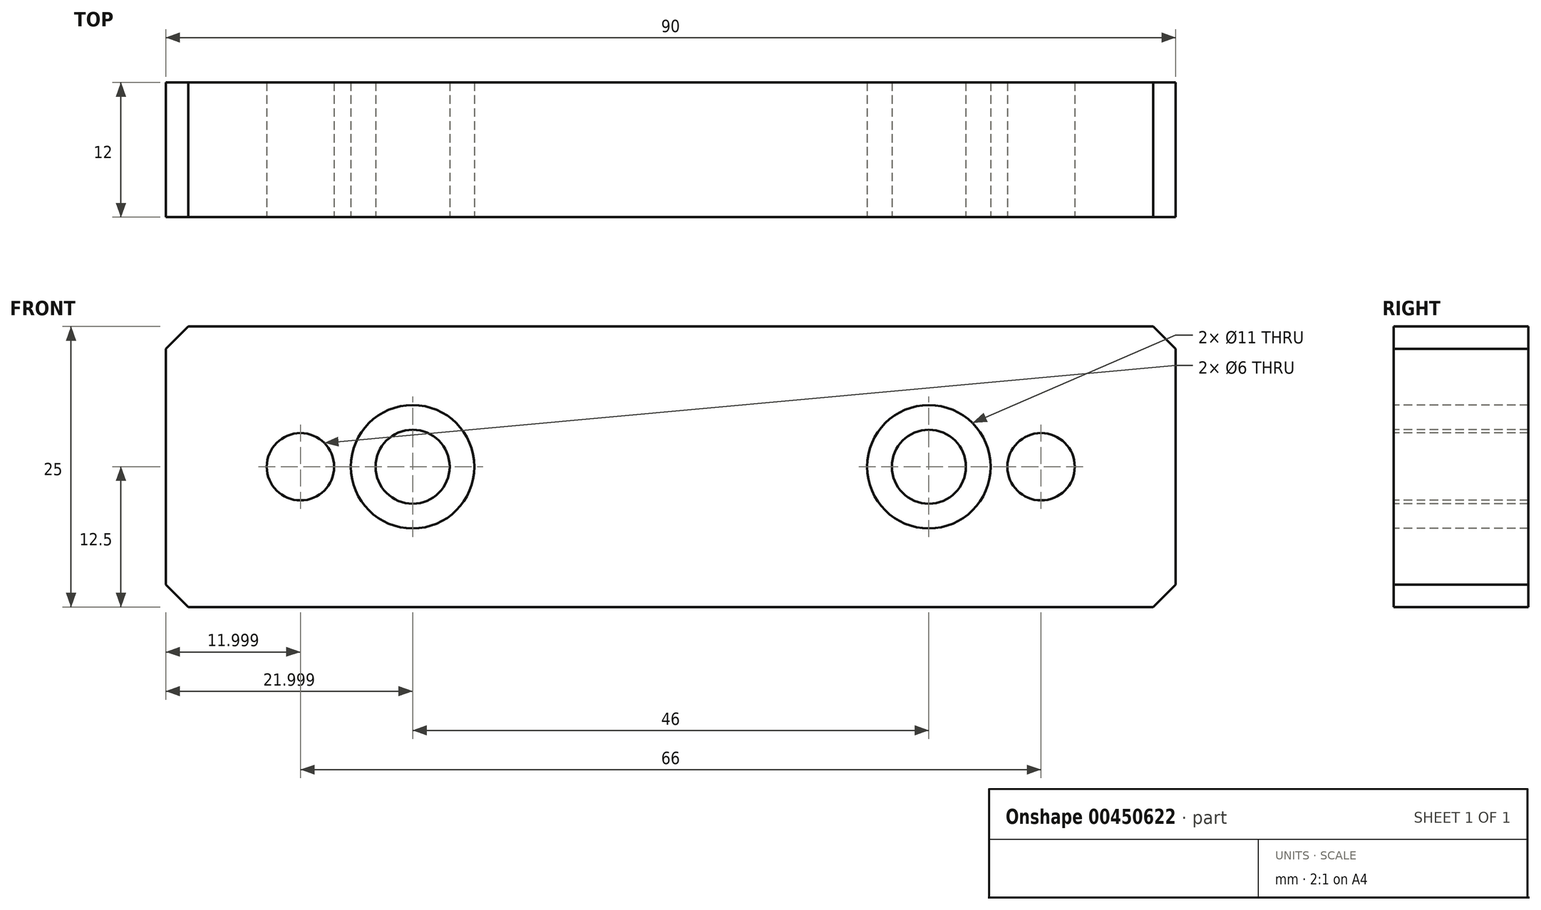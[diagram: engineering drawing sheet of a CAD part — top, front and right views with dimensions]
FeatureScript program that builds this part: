
annotation { "Feature Type Name" : "Feature", "Feature Type Description" : "" }
export const myFeature = defineFeature(function(context is Context, id is Id, definition is map)
    precondition{}
    {
        {
            var Q0;
            Q0=qCreatedBy(makeId("Front.planeOp"),FACE);
            var sketch = newSketch(context, id + "F0", { "sketchPlane" : qUnion([Q0])});
            skLineSegment(sketch, "E0", {"start": v(88.15, -90.29) * mm, "end": v(88.15, -111.29) * mm});
            skLineSegment(sketch, "E1", {"start": v(90.15, -88.29) * mm, "end": v(88.15, -90.29) * mm});
            skLineSegment(sketch, "E2", {"start": v(90.15, -113.29) * mm, "end": v(88.15, -111.29) * mm});
            skLineSegment(sketch, "E3", {"start": v(176.15, -88.29) * mm, "end": v(90.15, -88.29) * mm});
            skLineSegment(sketch, "E4", {"start": v(178.15, -90.29) * mm, "end": v(176.15, -88.29) * mm});
            skLineSegment(sketch, "E5", {"start": v(90.15, -113.29) * mm, "end": v(176.15, -113.29) * mm});
            skLineSegment(sketch, "E6", {"start": v(178.15, -111.29) * mm, "end": v(176.15, -113.29) * mm});
            skLineSegment(sketch, "E7", {"start": v(178.15, -111.29) * mm, "end": v(178.15, -90.29) * mm});
            skLineSegment(sketch, "E8", {"start": v(250.57, -113.29) * mm, "end": v(250.57, -88.29) * mm});
            skLineSegment(sketch, "E9", {"start": v(250.57, -88.29) * mm, "end": v(238.57, -88.29) * mm});
            skLineSegment(sketch, "E10", {"start": v(250.57, -113.29) * mm, "end": v(238.57, -113.29) * mm});
            skLineSegment(sketch, "E11", {"start": v(238.57, -88.29) * mm, "end": v(238.57, -113.29) * mm});
            skLineSegment(sketch, "E12", {"start": v(235.15, -100.79) * mm, "end": v(253.2, -100.79) * mm});
            skLineSegment(sketch, "E13", {"start": v(170.65, -100.79) * mm, "end": v(161.65, -100.79) * mm});
            skCircle(sketch, "E14", {"center": v(166.15, -100.79) * mm, "radius": 3 * mm});
            skLineSegment(sketch, "E15", {"start": v(166.15, -105.29) * mm, "end": v(166.15, -96.29) * mm});
            skCircle(sketch, "E16", {"center": v(166.15, -100.79) * mm, "radius": 2.46 * mm});
            skLineSegment(sketch, "E17", {"start": v(104.65, -100.79) * mm, "end": v(95.65, -100.79) * mm});
            skCircle(sketch, "E18", {"center": v(100.15, -100.79) * mm, "radius": 3 * mm});
            skLineSegment(sketch, "E19", {"start": v(100.15, -105.29) * mm, "end": v(100.15, -96.29) * mm});
            skCircle(sketch, "E20", {"center": v(100.15, -100.79) * mm, "radius": 2.46 * mm});
            skLineSegment(sketch, "E21", {"start": v(147.9, -100.79) * mm, "end": v(164.4, -100.79) * mm});
            skCircle(sketch, "E22", {"center": v(156.15, -100.79) * mm, "radius": 5.5 * mm});
            skLineSegment(sketch, "E23", {"start": v(156.15, -92.54) * mm, "end": v(156.15, -109.04) * mm});
            skCircle(sketch, "E24", {"center": v(156.15, -100.79) * mm, "radius": 3.3 * mm});
            skLineSegment(sketch, "E25", {"start": v(101.9, -100.79) * mm, "end": v(118.4, -100.79) * mm});
            skCircle(sketch, "E26", {"center": v(110.15, -100.79) * mm, "radius": 5.5 * mm});
            skLineSegment(sketch, "E27", {"start": v(110.15, -92.54) * mm, "end": v(110.15, -109.04) * mm});
            skCircle(sketch, "E28", {"center": v(110.15, -100.79) * mm, "radius": 3.3 * mm});
            skLineSegment(sketch, "E29", {"start": v(-261.09, -171.15) * mm, "end": v(-440.18, -171.15) * mm});
            skLineSegment(sketch, "E30", {"start": v(-440.18, -171.15) * mm, "end": v(-440.18, -94.4) * mm});
            skLineSegment(sketch, "E31", {"start": v(-440.18, -94.4) * mm, "end": v(-261.09, -94.4) * mm});
            skLineSegment(sketch, "E32", {"start": v(-261.09, -94.4) * mm, "end": v(-261.09, -171.15) * mm});
            skSolve(sketch);
        }
        {
            var Q0;
            Q0=makeQuery(id+"F0.imprint","IMPRINT",FACE,{"disambiguationData":[TD([[makeQuery(id+"F0.imprint","IMPRINT",EDGE,{"derivedFrom":sQuery(id+"F0.wireOp",EDGE,"E0")}),1.0]])]});
            var Q1;
            {var subQ0=sQuery(id+"F0.wireOp",EDGE,"E22");var subQ1=sQuery(id+"F0.wireOp",EDGE,"E21");var subQ2=makeQuery(id+"F0.imprint","INTERSECT",VERTEX,{"disambiguationData":[OD(1.0)],"derivedFrom":[subQ1,subQ0]});Q1=makeQuery(id+"F0.imprint","IMPRINT",FACE,{"disambiguationData":[TD([[makeQuery(id+"F0.imprint","IMPRINT",EDGE,{"disambiguationData":[TD([[subQ2,1.0]])],"derivedFrom":subQ1}),1.0]])]});}
            var Q2;
            {var subQ0=sQuery(id+"F0.wireOp",EDGE,"E22");var subQ1=sQuery(id+"F0.wireOp",EDGE,"E21");var subQ2=makeQuery(id+"F0.imprint","INTERSECT",VERTEX,{"disambiguationData":[OD(0.0)],"derivedFrom":[subQ1,subQ0]});Q2=makeQuery(id+"F0.imprint","IMPRINT",FACE,{"disambiguationData":[TD([[makeQuery(id+"F0.imprint","IMPRINT",EDGE,{"disambiguationData":[TD([[subQ2,-1.0]])],"derivedFrom":subQ1}),1.0]])]});}
            var Q3;
            {var subQ0=sQuery(id+"F0.wireOp",EDGE,"E22");var subQ1=sQuery(id+"F0.wireOp",EDGE,"E21");var subQ2=makeQuery(id+"F0.imprint","INTERSECT",VERTEX,{"disambiguationData":[OD(1.0)],"derivedFrom":[subQ1,subQ0]});Q3=makeQuery(id+"F0.imprint","IMPRINT",FACE,{"disambiguationData":[TD([[makeQuery(id+"F0.imprint","IMPRINT",EDGE,{"disambiguationData":[TD([[subQ2,1.0]])],"derivedFrom":subQ1}),-1.0]])]});}
            var Q4;
            {var subQ0=sQuery(id+"F0.wireOp",EDGE,"E23");var subQ1=sQuery(id+"F0.wireOp",EDGE,"E21");var subQ2=makeQuery(id+"F0.imprint","INTERSECT",VERTEX,{"derivedFrom":[subQ1,subQ0]});Q4=makeQuery(id+"F0.imprint","IMPRINT",FACE,{"disambiguationData":[TD([[makeQuery(id+"F0.imprint","IMPRINT",EDGE,{"disambiguationData":[TD([[subQ2,-1.0]])],"derivedFrom":subQ1}),1.0]])]});}
            var Q5;
            {var subQ0=sQuery(id+"F0.wireOp",EDGE,"E23");var subQ1=sQuery(id+"F0.wireOp",EDGE,"E21");var subQ2=makeQuery(id+"F0.imprint","INTERSECT",VERTEX,{"derivedFrom":[subQ1,subQ0]});Q5=makeQuery(id+"F0.imprint","IMPRINT",FACE,{"disambiguationData":[TD([[makeQuery(id+"F0.imprint","IMPRINT",EDGE,{"disambiguationData":[TD([[subQ2,-1.0]])],"derivedFrom":subQ1}),-1.0]])]});}
            var Q6;
            {var subQ0=sQuery(id+"F0.wireOp",EDGE,"E24");var subQ1=sQuery(id+"F0.wireOp",EDGE,"E21");var subQ2=makeQuery(id+"F0.imprint","INTERSECT",VERTEX,{"disambiguationData":[OD(0.0)],"derivedFrom":[subQ1,subQ0]});Q6=makeQuery(id+"F0.imprint","IMPRINT",FACE,{"disambiguationData":[TD([[makeQuery(id+"F0.imprint","IMPRINT",EDGE,{"disambiguationData":[TD([[subQ2,-1.0]])],"derivedFrom":subQ1}),1.0]])]});}
            var Q7;
            {var subQ0=sQuery(id+"F0.wireOp",EDGE,"E24");var subQ1=sQuery(id+"F0.wireOp",EDGE,"E21");var subQ2=makeQuery(id+"F0.imprint","INTERSECT",VERTEX,{"disambiguationData":[OD(0.0)],"derivedFrom":[subQ1,subQ0]});Q7=makeQuery(id+"F0.imprint","IMPRINT",FACE,{"disambiguationData":[TD([[makeQuery(id+"F0.imprint","IMPRINT",EDGE,{"disambiguationData":[TD([[subQ2,-1.0]])],"derivedFrom":subQ1}),-1.0]])]});}
            var Q8;
            {var subQ0=sQuery(id+"F0.wireOp",EDGE,"E22");var subQ1=sQuery(id+"F0.wireOp",EDGE,"E21");var subQ2=makeQuery(id+"F0.imprint","INTERSECT",VERTEX,{"disambiguationData":[OD(0.0)],"derivedFrom":[subQ1,subQ0]});Q8=makeQuery(id+"F0.imprint","IMPRINT",FACE,{"disambiguationData":[TD([[makeQuery(id+"F0.imprint","IMPRINT",EDGE,{"disambiguationData":[TD([[subQ2,-1.0]])],"derivedFrom":subQ1}),-1.0]])]});}
            var Q9;
            {var subQ0=sQuery(id+"F0.wireOp",EDGE,"E27");var subQ1=sQuery(id+"F0.wireOp",EDGE,"E25");var subQ2=makeQuery(id+"F0.imprint","INTERSECT",VERTEX,{"derivedFrom":[subQ1,subQ0]});Q9=makeQuery(id+"F0.imprint","IMPRINT",FACE,{"disambiguationData":[TD([[makeQuery(id+"F0.imprint","IMPRINT",EDGE,{"disambiguationData":[TD([[subQ2,-1.0]])],"derivedFrom":subQ1}),1.0]])]});}
            var Q10;
            {var subQ0=sQuery(id+"F0.wireOp",EDGE,"E26");var subQ1=sQuery(id+"F0.wireOp",EDGE,"E25");var subQ2=makeQuery(id+"F0.imprint","INTERSECT",VERTEX,{"disambiguationData":[OD(1.0)],"derivedFrom":[subQ1,subQ0]});Q10=makeQuery(id+"F0.imprint","IMPRINT",FACE,{"disambiguationData":[TD([[makeQuery(id+"F0.imprint","IMPRINT",EDGE,{"disambiguationData":[TD([[subQ2,1.0]])],"derivedFrom":subQ1}),-1.0]])]});}
            var Q11;
            {var subQ0=sQuery(id+"F0.wireOp",EDGE,"E27");var subQ1=sQuery(id+"F0.wireOp",EDGE,"E25");var subQ2=makeQuery(id+"F0.imprint","INTERSECT",VERTEX,{"derivedFrom":[subQ1,subQ0]});Q11=makeQuery(id+"F0.imprint","IMPRINT",FACE,{"disambiguationData":[TD([[makeQuery(id+"F0.imprint","IMPRINT",EDGE,{"disambiguationData":[TD([[subQ2,-1.0]])],"derivedFrom":subQ1}),-1.0]])]});}
            var Q12;
            {var subQ0=sQuery(id+"F0.wireOp",EDGE,"E26");var subQ1=sQuery(id+"F0.wireOp",EDGE,"E25");var subQ2=makeQuery(id+"F0.imprint","INTERSECT",VERTEX,{"disambiguationData":[OD(1.0)],"derivedFrom":[subQ1,subQ0]});Q12=makeQuery(id+"F0.imprint","IMPRINT",FACE,{"disambiguationData":[TD([[makeQuery(id+"F0.imprint","IMPRINT",EDGE,{"disambiguationData":[TD([[subQ2,1.0]])],"derivedFrom":subQ1}),1.0]])]});}
            var Q13;
            {var subQ0=sQuery(id+"F0.wireOp",EDGE,"E28");var subQ1=sQuery(id+"F0.wireOp",EDGE,"E25");var subQ2=makeQuery(id+"F0.imprint","INTERSECT",VERTEX,{"disambiguationData":[OD(0.0)],"derivedFrom":[subQ1,subQ0]});Q13=makeQuery(id+"F0.imprint","IMPRINT",FACE,{"disambiguationData":[TD([[makeQuery(id+"F0.imprint","IMPRINT",EDGE,{"disambiguationData":[TD([[subQ2,-1.0]])],"derivedFrom":subQ1}),-1.0]])]});}
            var Q14;
            {var subQ0=sQuery(id+"F0.wireOp",EDGE,"E26");var subQ1=sQuery(id+"F0.wireOp",EDGE,"E25");var subQ2=makeQuery(id+"F0.imprint","INTERSECT",VERTEX,{"disambiguationData":[OD(0.0)],"derivedFrom":[subQ1,subQ0]});Q14=makeQuery(id+"F0.imprint","IMPRINT",FACE,{"disambiguationData":[TD([[makeQuery(id+"F0.imprint","IMPRINT",EDGE,{"disambiguationData":[TD([[subQ2,-1.0]])],"derivedFrom":subQ1}),-1.0]])]});}
            var Q15;
            {var subQ0=sQuery(id+"F0.wireOp",EDGE,"E28");var subQ1=sQuery(id+"F0.wireOp",EDGE,"E25");var subQ2=makeQuery(id+"F0.imprint","INTERSECT",VERTEX,{"disambiguationData":[OD(0.0)],"derivedFrom":[subQ1,subQ0]});Q15=makeQuery(id+"F0.imprint","IMPRINT",FACE,{"disambiguationData":[TD([[makeQuery(id+"F0.imprint","IMPRINT",EDGE,{"disambiguationData":[TD([[subQ2,-1.0]])],"derivedFrom":subQ1}),1.0]])]});}
            var Q16;
            {var subQ0=sQuery(id+"F0.wireOp",EDGE,"E26");var subQ1=sQuery(id+"F0.wireOp",EDGE,"E25");var subQ2=makeQuery(id+"F0.imprint","INTERSECT",VERTEX,{"disambiguationData":[OD(0.0)],"derivedFrom":[subQ1,subQ0]});Q16=makeQuery(id+"F0.imprint","IMPRINT",FACE,{"disambiguationData":[TD([[makeQuery(id+"F0.imprint","IMPRINT",EDGE,{"disambiguationData":[TD([[subQ2,-1.0]])],"derivedFrom":subQ1}),1.0]])]});}
            extrude(context, id + "F1", {"entities" : qUnion([Q0, Q1, Q2, Q3, Q4, Q5, Q6, Q7, Q8, Q9, Q10, Q11, Q12, Q13, Q14, Q15, Q16]), "oppositeDirection" : true, "depth" : 12 * mm});
        }
        {
            var Q0;
            Q0=sQuery(id+"F0.wireOp",VERTEX,"E22.center");
            var Q1;
            Q1=sQuery(id+"F0.wireOp",VERTEX,"E28.center");
            var Q2;
            Q2=makeQuery(id+"F1.opExtrude","SWEPT_BODY",BODY,{"disambiguationData":[OSD([sQuery(id+"F0.wireOp",EDGE,"E0"),sQuery(id+"F0.wireOp",EDGE,"E1"),sQuery(id+"F0.wireOp",EDGE,"E2"),sQuery(id+"F0.wireOp",EDGE,"E3"),sQuery(id+"F0.wireOp",EDGE,"E4"),sQuery(id+"F0.wireOp",EDGE,"E5"),sQuery(id+"F0.wireOp",EDGE,"E6"),sQuery(id+"F0.wireOp",EDGE,"E7"),sQuery(id+"F0.wireOp",EDGE,"E14"),sQuery(id+"F0.wireOp",EDGE,"E18")])]});
            hole(context, id + "F2", {"style" : HoleStyle.C_BORE, "endStyle" : HoleEndStyle.THROUGH, "holeDiameter" : 6.6 * mm, "cBoreDiameter" : 11 * mm, "cBoreDepth" : 8 * mm, "isTappedThrough" : true, "tappedDepth" : 12 * mm, "tapClearance" : 3, "locations" : qUnion([Q0, Q1]), "scope" : qUnion([Q2])});
        }
    });
